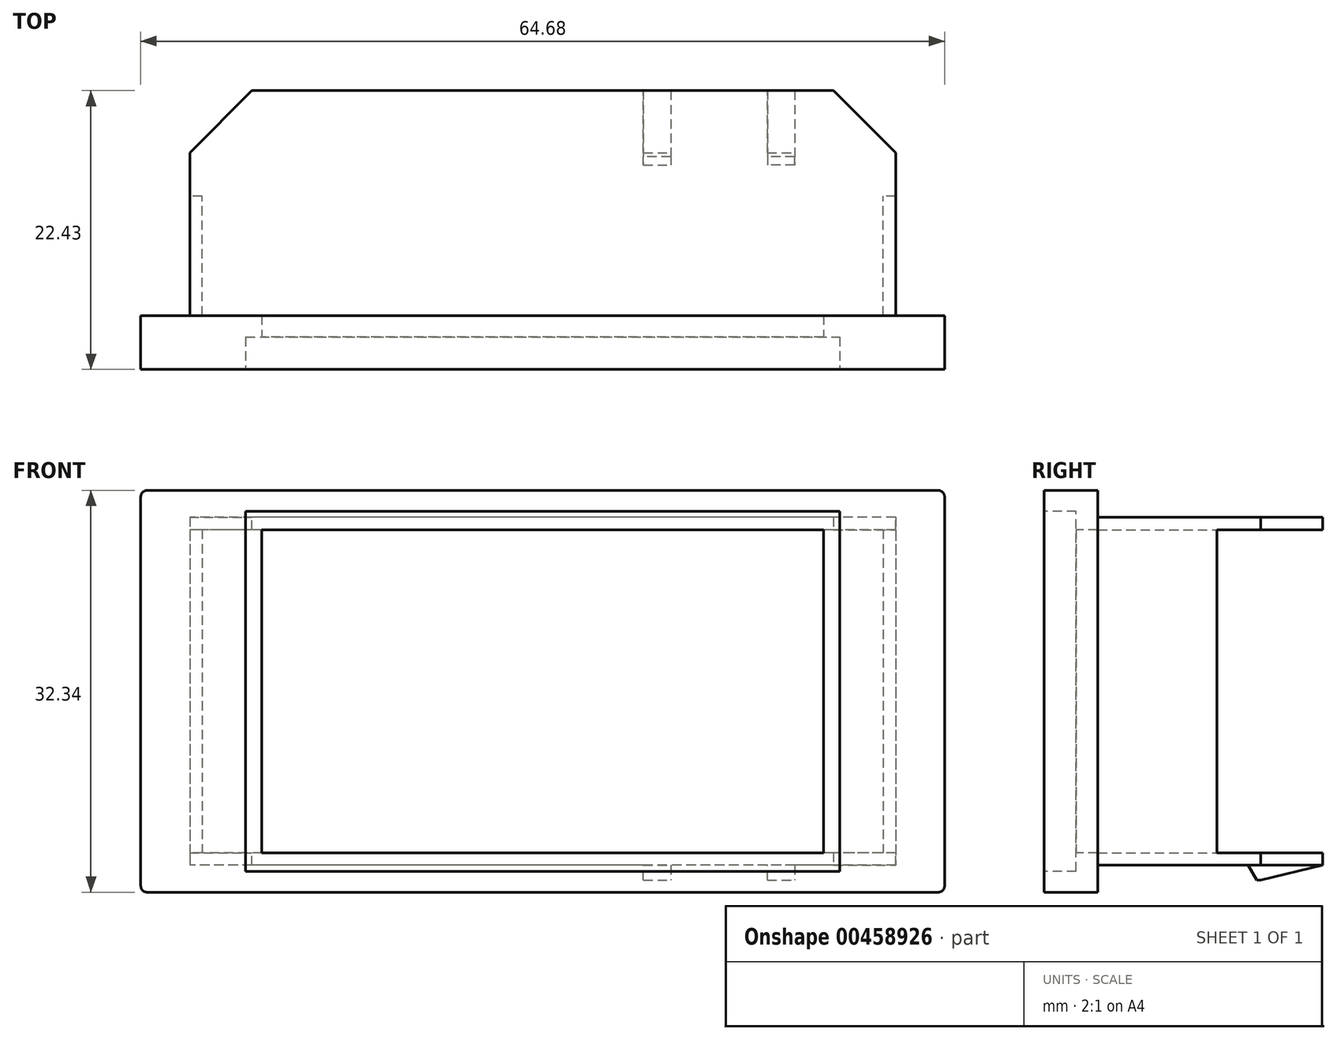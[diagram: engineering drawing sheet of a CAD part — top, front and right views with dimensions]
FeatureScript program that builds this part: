
annotation { "Feature Type Name" : "Feature", "Feature Type Description" : "" }
export const myFeature = defineFeature(function(context is Context, id is Id, definition is map)
    precondition{}
    {
        {
            var Q0;
            Q0=qCreatedBy(makeId("Front.planeOp"),FACE);
            var sketch = newSketch(context, id + "F0", { "sketchPlane" : qUnion([Q0])});
            skLineSegment(sketch, "E0.bottom", {"start": v(-32.34, 16.17) * mm, "end": v(32.34, 16.17) * mm});
            skLineSegment(sketch, "E0.top", {"start": v(-32.34, -16.17) * mm, "end": v(32.34, -16.17) * mm});
            skLineSegment(sketch, "E0.left", {"start": v(-32.34, 16.17) * mm, "end": v(-32.34, -16.17) * mm});
            skLineSegment(sketch, "E0.right", {"start": v(32.34, 16.17) * mm, "end": v(32.34, -16.17) * mm});
            skSolve(sketch);
        }
        {
            var Q0;
            Q0 = qSketchRegion(id + "F0", true);
            extrude(context, id + "F1", {"entities" : qUnion([Q0]), "depth" : 4.33 * mm});
        }
        {
            var Q0;
            Q0=makeQuery(id+"F1.opExtrude","SWEPT_EDGE",EDGE,{"disambiguationData":[OSD([sQuery(id+"F0.wireOp",EDGE,"E0.bottom"),sQuery(id+"F0.wireOp",EDGE,"E0.left")])]});
            var Q1;
            Q1=makeQuery(id+"F1.opExtrude","SWEPT_EDGE",EDGE,{"disambiguationData":[OSD([sQuery(id+"F0.wireOp",EDGE,"E0.top"),sQuery(id+"F0.wireOp",EDGE,"E0.left")])]});
            var Q2;
            Q2=makeQuery(id+"F1.opExtrude","SWEPT_EDGE",EDGE,{"disambiguationData":[OSD([sQuery(id+"F0.wireOp",EDGE,"E0.bottom"),sQuery(id+"F0.wireOp",EDGE,"E0.right")])]});
            var Q3;
            Q3=makeQuery(id+"F1.opExtrude","SWEPT_EDGE",EDGE,{"disambiguationData":[OSD([sQuery(id+"F0.wireOp",EDGE,"E0.top"),sQuery(id+"F0.wireOp",EDGE,"E0.right")])]});
            fillet(context, id + "F2", {"entities" : qUnion([Q0, Q1, Q2, Q3]), "radius" : .5 * mm, "tangentPropagation" : true, "allowEdgeOverflow" : false});
        }
        {
            var Q0;
            Q0=makeQuery(id+"F1.opExtrude","CAP_FACE",FACE,{"disambiguationData":[OSD([sQuery(id+"F0.wireOp",EDGE,"E0.bottom"),sQuery(id+"F0.wireOp",EDGE,"E0.top"),sQuery(id+"F0.wireOp",EDGE,"E0.left"),sQuery(id+"F0.wireOp",EDGE,"E0.right")])],"isStart":true});
            var sketch = newSketch(context, id + "F3", { "sketchPlane" : qUnion([Q0])});
            skLineSegment(sketch, "E1.bottom", {"start": v(-28.4, 14) * mm, "end": v(28.4, 14) * mm});
            skLineSegment(sketch, "E1.top", {"start": v(-28.4, -14) * mm, "end": v(28.4, -14) * mm});
            skLineSegment(sketch, "E1.left", {"start": v(-28.4, 14) * mm, "end": v(-28.4, -14) * mm});
            skLineSegment(sketch, "E1.right", {"start": v(28.4, 14) * mm, "end": v(28.4, -14) * mm});
            skSolve(sketch);
        }
        {
            var Q0;
            Q0 = qSketchRegion(id + "F3", true);
            extrude(context, id + "F4", {"entities" : qUnion([Q0]), "operationType" : NewBodyOperationType.ADD, "depth" : 9.6 * mm});
        }
        {
            var Q0;
            Q0=makeQuery(id+"F4.opExtrude","CAP_FACE",FACE,{"disambiguationData":[OSD([sQuery(id+"F3.wireOp",EDGE,"E1.bottom"),sQuery(id+"F3.wireOp",EDGE,"E1.top"),sQuery(id+"F3.wireOp",EDGE,"E1.left"),sQuery(id+"F3.wireOp",EDGE,"E1.right")])],"isStart":false});
            var sketch = newSketch(context, id + "F5", { "sketchPlane" : qUnion([Q0])});
            skLineSegment(sketch, "E2.0", {"start": v(-27.4, 13) * mm, "end": v(27.4, 13) * mm});
            skLineSegment(sketch, "E2.1", {"start": v(-27.4, 13) * mm, "end": v(-27.4, -13) * mm});
            skLineSegment(sketch, "E2.2", {"start": v(-27.4, -13) * mm, "end": v(27.4, -13) * mm});
            skLineSegment(sketch, "E2.3", {"start": v(27.4, 13) * mm, "end": v(27.4, -13) * mm});
            skSolve(sketch);
        }
        {
            var Q0;
            Q0=makeQuery(id+"F5.imprint","IMPRINT",FACE,{"disambiguationData":[TD([[makeQuery(id+"F5.imprint","IMPRINT",EDGE,{"derivedFrom":sQuery(id+"F5.wireOp",EDGE,"E2.0")}),-1.0]])]});
            var Q1;
            Q1=makeQuery(id+"F1.opExtrude","CAP_FACE",FACE,{"disambiguationData":[OSD([sQuery(id+"F0.wireOp",EDGE,"E0.bottom"),sQuery(id+"F0.wireOp",EDGE,"E0.top"),sQuery(id+"F0.wireOp",EDGE,"E0.left"),sQuery(id+"F0.wireOp",EDGE,"E0.right")])],"isStart":true});
            extrude(context, id + "F6", {"entities" : qUnion([Q0]), "operationType" : NewBodyOperationType.REMOVE, "endBound" : BoundingType.UP_TO_SURFACE, "oppositeDirection" : true, "endBoundEntityFace" : qUnion([Q1]), "depth" : 25 * mm});
        }
        {
            var Q0;
            Q0=makeQuery(id+"F4.opExtrude","CAP_FACE",FACE,{"disambiguationData":[OSD([sQuery(id+"F3.wireOp",EDGE,"E1.bottom"),sQuery(id+"F3.wireOp",EDGE,"E1.top"),sQuery(id+"F3.wireOp",EDGE,"E1.left"),sQuery(id+"F3.wireOp",EDGE,"E1.right")])],"isStart":false});
            var sketch = newSketch(context, id + "F7", { "sketchPlane" : qUnion([Q0])});
            skLineSegment(sketch, "E3.bottom", {"start": v(-28.4, 14) * mm, "end": v(28.4, 14) * mm});
            skLineSegment(sketch, "E3.top", {"start": v(-28.4, 13) * mm, "end": v(28.4, 13) * mm});
            skLineSegment(sketch, "E3.left", {"start": v(-28.4, 14) * mm, "end": v(-28.4, 13) * mm});
            skLineSegment(sketch, "E3.right", {"start": v(28.4, 14) * mm, "end": v(28.4, 13) * mm});
            skLineSegment(sketch, "E4.bottom", {"start": v(-28.4, -14) * mm, "end": v(28.4, -14) * mm});
            skLineSegment(sketch, "E4.top", {"start": v(-28.4, -13) * mm, "end": v(28.4, -13) * mm});
            skLineSegment(sketch, "E4.left", {"start": v(-28.4, -14) * mm, "end": v(-28.4, -13) * mm});
            skLineSegment(sketch, "E4.right", {"start": v(28.4, -14) * mm, "end": v(28.4, -13) * mm});
            skSolve(sketch);
        }
        {
            var Q0;
            Q0 = qSketchRegion(id + "F7", true);
            extrude(context, id + "F8", {"entities" : qUnion([Q0]), "operationType" : NewBodyOperationType.ADD, "depth" : 8.5 * mm});
        }
        {
            var Q0;
            Q0=makeQuery(id+"F8.opExtrude","CAP_EDGE",EDGE,{"disambiguationData":[OSD([sQuery(id+"F7.wireOp",EDGE,"E4.left")])],"isStart":false});
            var Q1;
            Q1=makeQuery(id+"F8.opExtrude","CAP_EDGE",EDGE,{"disambiguationData":[OSD([sQuery(id+"F7.wireOp",EDGE,"E3.left")])],"isStart":false});
            var Q2;
            Q2=makeQuery(id+"F8.opExtrude","CAP_EDGE",EDGE,{"disambiguationData":[OSD([sQuery(id+"F7.wireOp",EDGE,"E4.right")])],"isStart":false});
            var Q3;
            Q3=makeQuery(id+"F8.opExtrude","CAP_EDGE",EDGE,{"disambiguationData":[OSD([sQuery(id+"F7.wireOp",EDGE,"E3.right")])],"isStart":false});
            chamfer(context, id + "F9", {"entities" : qUnion([Q0, Q1, Q2, Q3]), "width" : 5 * mm, "tangentPropagation" : true});
        }
        {
            var Q0;
            Q0=makeQuery(id+"F8.boolean.opBoolean","MERGE",FACE,{"derivedFrom":[makeQuery(id+"F4.opExtrude","SWEPT_FACE",FACE,{"disambiguationData":[OSD([sQuery(id+"F3.wireOp",EDGE,"E1.top")])]}),makeQuery(id+"F8.opExtrude","SWEPT_FACE",FACE,{"disambiguationData":[OSD([sQuery(id+"F7.wireOp",EDGE,"E4.bottom")])]})]});
            var sketch = newSketch(context, id + "F10", { "sketchPlane" : qUnion([Q0])});
            skLineSegment(sketch, "E5.bottom", {"start": v(20.29, -18.1) * mm, "end": v(18.09, -18.1) * mm});
            skLineSegment(sketch, "E5.top", {"start": v(20.29, -12.1) * mm, "end": v(18.09, -12.1) * mm});
            skLineSegment(sketch, "E5.left", {"start": v(20.29, -18.1) * mm, "end": v(20.29, -12.1) * mm});
            skLineSegment(sketch, "E5.right", {"start": v(18.09, -18.1) * mm, "end": v(18.09, -12.1) * mm});
            skLineSegment(sketch, "E6.bottom", {"start": v(8.1, -18.1) * mm, "end": v(10.3, -18.1) * mm});
            skLineSegment(sketch, "E6.top", {"start": v(8.1, -12.1) * mm, "end": v(10.3, -12.1) * mm});
            skLineSegment(sketch, "E6.left", {"start": v(8.1, -18.1) * mm, "end": v(8.1, -12.1) * mm});
            skLineSegment(sketch, "E6.right", {"start": v(10.3, -18.1) * mm, "end": v(10.3, -12.1) * mm});
            skLineSegment(sketch, "E7", {"start": v(14.2, 1.65) * mm, "end": v(14.2, -22.8) * mm, "construction": true});
            skSolve(sketch);
        }
        {
            var Q0;
            Q0 = qSketchRegion(id + "F10", true);
            extrude(context, id + "F11", {"entities" : qUnion([Q0]), "operationType" : NewBodyOperationType.ADD, "depth" : 1.2 * mm});
        }
        {
            var Q0;
            Q0=makeQuery(id+"F11.opExtrude","CAP_EDGE",EDGE,{"disambiguationData":[OSD([sQuery(id+"F10.wireOp",EDGE,"E5.top")])],"isStart":false});
            chamfer(context, id + "F12", {"entities" : qUnion([Q0]), "chamferType" : ChamferType.OFFSET_ANGLE, "width" : 1.2 * mm, "oppositeDirection" : true, "angle" : 30 * degree, "tangentPropagation" : true});
        }
        {
            var Q0;
            Q0=makeQuery(id+"F11.opExtrude","CAP_EDGE",EDGE,{"disambiguationData":[OSD([sQuery(id+"F10.wireOp",EDGE,"E6.top")])],"isStart":false});
            chamfer(context, id + "F13", {"entities" : qUnion([Q0]), "chamferType" : ChamferType.OFFSET_ANGLE, "width" : 1.2 * mm, "oppositeDirection" : false, "angle" : 30 * degree, "tangentPropagation" : true});
        }
        {
            var Q0;
            Q0=makeQuery(id+"F11.opExtrude","CAP_EDGE",EDGE,{"disambiguationData":[OSD([sQuery(id+"F10.wireOp",EDGE,"E6.bottom")])],"isStart":false});
            var Q1;
            Q1=makeQuery(id+"F11.opExtrude","CAP_EDGE",EDGE,{"disambiguationData":[OSD([sQuery(id+"F10.wireOp",EDGE,"E5.bottom")])],"isStart":false});
            chamfer(context, id + "F14", {"entities" : qUnion([Q0, Q1]), "chamferType" : ChamferType.TWO_OFFSETS, "width1" : 1.2 * mm, "oppositeDirection" : false, "width2" : 5 * mm, "tangentPropagation" : true});
        }
        {
            var Q0;
            Q0=makeQuery(id+"F1.opExtrude","CAP_FACE",FACE,{"disambiguationData":[OSD([sQuery(id+"F0.wireOp",EDGE,"E0.bottom"),sQuery(id+"F0.wireOp",EDGE,"E0.top"),sQuery(id+"F0.wireOp",EDGE,"E0.left"),sQuery(id+"F0.wireOp",EDGE,"E0.right")])],"isStart":false});
            var sketch = newSketch(context, id + "F15", { "sketchPlane" : qUnion([Q0])});
            skLineSegment(sketch, "E8.bottom", {"start": v(-23.9, -14.5) * mm, "end": v(23.9, -14.5) * mm});
            skLineSegment(sketch, "E8.top", {"start": v(-23.9, 14.5) * mm, "end": v(23.9, 14.5) * mm});
            skLineSegment(sketch, "E8.left", {"start": v(-23.9, -14.5) * mm, "end": v(-23.9, 14.5) * mm});
            skLineSegment(sketch, "E8.right", {"start": v(23.9, -14.5) * mm, "end": v(23.9, 14.5) * mm});
            skPoint(sketch, "E8.middle", {"position": v(0, 0) * mm});
            skSolve(sketch);
        }
        {
            var Q0;
            Q0=makeQuery(id+"F15.imprint","IMPRINT",FACE,{"disambiguationData":[TD([[makeQuery(id+"F15.imprint","IMPRINT",EDGE,{"derivedFrom":sQuery(id+"F15.wireOp",EDGE,"E8.bottom")}),1.0]])]});
            extrude(context, id + "F16", {"entities" : qUnion([Q0]), "operationType" : NewBodyOperationType.REMOVE, "oppositeDirection" : true, "depth" : 2.6 * mm});
        }
        {
            var Q0;
            Q0=makeQuery(id+"F16.boolean.opBoolean","COPY",FACE,{"derivedFrom":makeQuery(id+"F16.opExtrude","CAP_FACE",FACE,{"disambiguationData":[OSD([sQuery(id+"F15.wireOp",EDGE,"E8.bottom"),sQuery(id+"F15.wireOp",EDGE,"E8.top"),sQuery(id+"F15.wireOp",EDGE,"E8.left"),sQuery(id+"F15.wireOp",EDGE,"E8.right")])],"isStart":false})});
            var sketch = newSketch(context, id + "F17", { "sketchPlane" : qUnion([Q0])});
            skLineSegment(sketch, "E9.bottom", {"start": v(22.6, 13) * mm, "end": v(-22.6, 13) * mm});
            skLineSegment(sketch, "E9.top", {"start": v(22.6, -13) * mm, "end": v(-22.6, -13) * mm});
            skLineSegment(sketch, "E9.left", {"start": v(22.6, 13) * mm, "end": v(22.6, -13) * mm});
            skLineSegment(sketch, "E9.right", {"start": v(-22.6, 13) * mm, "end": v(-22.6, -13) * mm});
            skPoint(sketch, "E9.middle", {"position": v(0, 0) * mm});
            skSolve(sketch);
        }
        {
            var Q0;
            Q0 = qSketchRegion(id + "F17", true);
            extrude(context, id + "F18", {"entities" : qUnion([Q0]), "operationType" : NewBodyOperationType.REMOVE, "oppositeDirection" : true, "depth" : 25 * mm});
        }
    });
